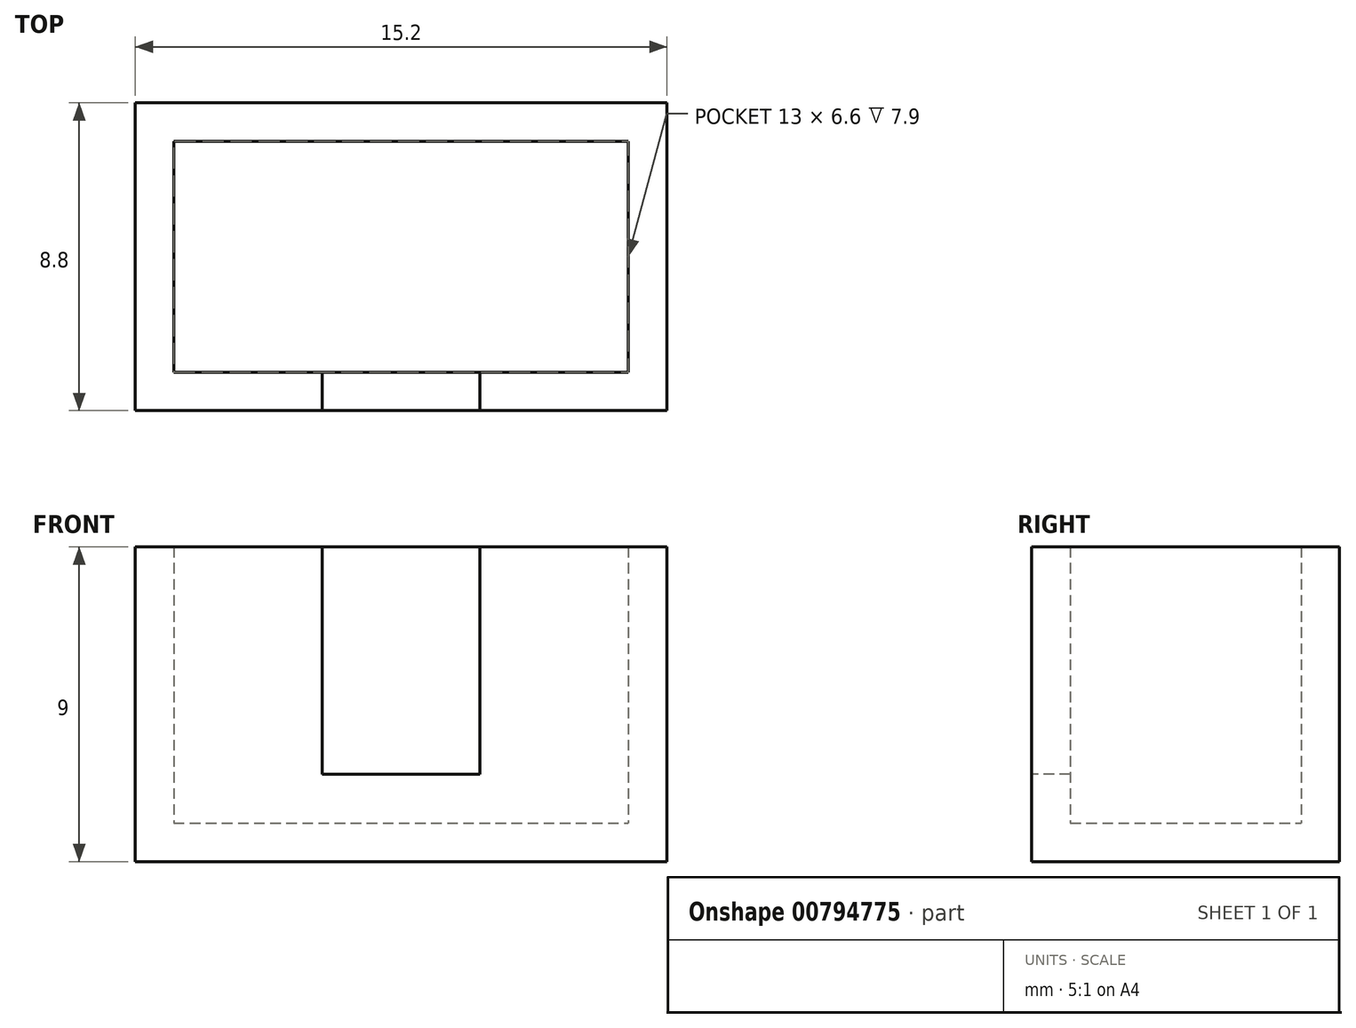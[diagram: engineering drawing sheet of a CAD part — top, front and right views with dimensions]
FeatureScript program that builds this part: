
annotation { "Feature Type Name" : "Feature", "Feature Type Description" : "" }
export const myFeature = defineFeature(function(context is Context, id is Id, definition is map)
    precondition{}
    {
        {
            var Q0;
            Q0=qCreatedBy(makeId("Top.planeOp"),FACE);
            var sketch = newSketch(context, id + "F0", { "sketchPlane" : qUnion([Q0])});
            skLineSegment(sketch, "E0.bottom", {"start": v(0, 0) * mm, "end": v(15.2, 0) * mm});
            skLineSegment(sketch, "E0.top", {"start": v(0, 8.8) * mm, "end": v(15.2, 8.8) * mm});
            skLineSegment(sketch, "E0.left", {"start": v(0, 0) * mm, "end": v(0, 8.8) * mm});
            skLineSegment(sketch, "E0.right", {"start": v(15.2, 0) * mm, "end": v(15.2, 8.8) * mm});
            skSolve(sketch);
        }
        {
            var Q0;
            Q0=makeQuery(id+"F0.imprint","IMPRINT",FACE,{"disambiguationData":[TD([[makeQuery(id+"F0.imprint","IMPRINT",EDGE,{"derivedFrom":sQuery(id+"F0.wireOp",EDGE,"E0.bottom")}),1.0]])]});
            extrude(context, id + "F1", {"entities" : qUnion([Q0]), "depth" : 9 * mm, "offsetDistance" : 25 * mm});
        }
        {
            var Q0;
            Q0=makeQuery(id+"F1.opExtrude","CAP_FACE",FACE,{"disambiguationData":[OSD([sQuery(id+"F0.wireOp",EDGE,"E0.bottom"),sQuery(id+"F0.wireOp",EDGE,"E0.top"),sQuery(id+"F0.wireOp",EDGE,"E0.left"),sQuery(id+"F0.wireOp",EDGE,"E0.right")])],"isStart":false});
            shell(context, id + "F2", {"entities" : qUnion([Q0]), "thickness" : 1.1 * mm});
        }
        {
            var Q0;
            Q0=makeQuery(id+"F1.opExtrude","SWEPT_FACE",FACE,{"disambiguationData":[OSD([sQuery(id+"F0.wireOp",EDGE,"E0.bottom")])]});
            var sketch = newSketch(context, id + "F3", { "sketchPlane" : qUnion([Q0])});
            skLineSegment(sketch, "E1", {"start": v(7.6, 11.28) * mm, "end": v(7.6, -1.72) * mm, "construction": true});
            skPoint(sketch, "E1.startSnap0", {"position": v(7.6, 9) * mm});
            skLineSegment(sketch, "E2.bottom", {"start": v(5.35, 9) * mm, "end": v(9.85, 9) * mm});
            skLineSegment(sketch, "E2.top", {"start": v(5.35, 2.5) * mm, "end": v(9.85, 2.5) * mm});
            skLineSegment(sketch, "E2.left", {"start": v(5.35, 9) * mm, "end": v(5.35, 2.5) * mm});
            skLineSegment(sketch, "E2.right", {"start": v(9.85, 9) * mm, "end": v(9.85, 2.5) * mm});
            skSolve(sketch);
        }
        {
            var Q0;
            Q0=makeQuery(id+"F3.imprint","IMPRINT",FACE,{"disambiguationData":[TD([[makeQuery(id+"F3.imprint","IMPRINT",EDGE,{"derivedFrom":sQuery(id+"F3.wireOp",EDGE,"E2.bottom")}),-1.0]])]});
            extrude(context, id + "F4", {"entities" : qUnion([Q0]), "operationType" : NewBodyOperationType.REMOVE, "endBound" : BoundingType.UP_TO_NEXT, "oppositeDirection" : true, "depth" : 25 * mm, "offsetDistance" : 25 * mm});
        }
    });
